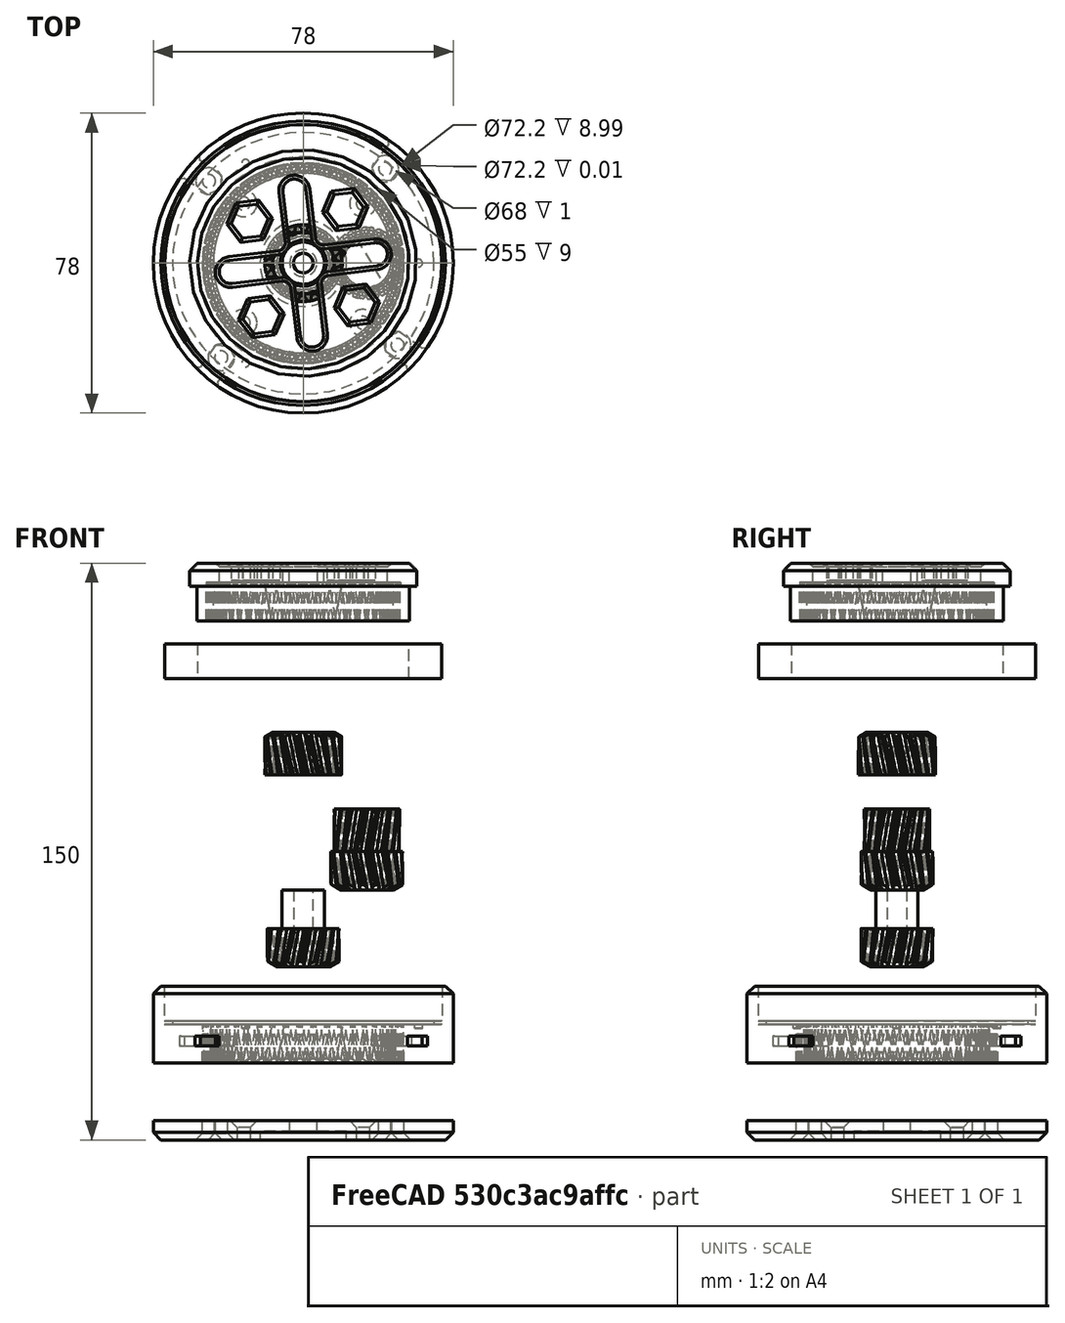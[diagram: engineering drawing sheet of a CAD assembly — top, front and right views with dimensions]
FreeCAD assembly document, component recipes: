
FREECAD ASSEMBLY — COMPONENT RECIPES ("gearbox-v3-helical")

This assembly document has 8 components, labeled P0..P7 below (a component is one placed body or linked part). 8 of them carry a construction recipe — the FreeCAD feature program that regenerates the part from scratch, quoted from this document or its linked companion documents; the rest are supplied as boundary geometry only. No exploded tour is included for this assembly.
COMPONENT P0 — recipe-attached ("S1-Sun", modeled in this document).
Construction recipe (the document's own serialized feature program — sketch geometry with constraints, then the solid features built on it; lengths are millimeters unless a unit is written):

FEATURE [Sketcher::SketchObject] Sketch008
  FullyConstrained = true
  MapMode = 5
  Support = -> [XY_Plane]
  TreeRank = 144
  sketch-geometry (1):
    g0: Circle CenterX=0 CenterY=0 CenterZ=0 NormalX=0 NormalY=0 NormalZ=1 AngleXU=0 Radius=2.55
  constraints (2):
    c: Coincident(g0,g-1)
    c: Diameter(g0) = 5.1
FEATURE [Part::Part2DObjectPython] InvoluteGear  label="s1-sun-gear"  # Draft 2D object (typed FeaturePython)
  ExternalGear = true
  HighPrecision = false
  Modules = 1.1
  NumberOfTeeth = 15
  PressureAngle = 20
  TreeRank = 283
  expr: Modules = <<sp>>.s1_module
  expr: NumberOfTeeth = <<sp>>.s1sun_teeth
FEATURE [PartDesign::AdditiveHelix] Helix003
  AddSubType = 0
  Angle = 0
  Axis = (-3e-16,3e-16,1)
  Base = (0,0,0)
  ClaimChildren = false
  Fit = 0
  FitJoin = 0
  Growth = 0
  HasBeenEdited = true
  Height = 10
  InnerFit = 0
  InnerFitJoin = 0
  LeftHanded = false
  Linearize = true
  Mode = 0
  NewSolid = false
  Outside = false
  Pitch = 250
  Profile = -> InvoluteGear
  ReferenceAxis = -> Z_Axis
  Suppress = false
  TreeRank = 284
  Turns = 0.04
  _ProfileBasedVersion = 1
FEATURE [PartDesign::Pocket] Pocket005
  AddSubType = 1
  BaseFeature = -> Helix003
  CheckUpToFaceLimits = true
  ClaimChildren = false
  Fit = 0
  FitJoin = 0
  InnerFit = 0
  InnerFitJoin = 0
  InnerTaperAngle = 0
  InnerTaperAngleRev = 0
  Length = 20
  Length2 = 20
  Linearize = true
  NewSolid = false
  Profile = -> Sketch008
  Reversed = true
  Suppress = false
  TreeRank = 145
  Type = 4
  _ProfileBasedVersion = 1
  _Version = 1
FEATURE [Sketcher::SketchObject] Sketch009
  FullyConstrained = true
  MapMode = 5
  Placement = pos=(3.3597e-05,5.68264e-05,10) rot=(-0.860809,0.508928,-1e-06;7e-06rad)
  Support = -> [Pocket005]
  TreeRank = 146
  sketch-geometry (2):
    g0: Circle CenterX=0 CenterY=0 CenterZ=0 NormalX=0 NormalY=0 NormalZ=1 AngleXU=0 Radius=2.55
    g1: Circle CenterX=0 CenterY=0 CenterZ=0 NormalX=0 NormalY=0 NormalZ=1 AngleXU=0 Radius=5.5
  constraints (4):
    c: Coincident(g0,g-1)
    c: Coincident(g1,g0)
    c: Diameter(g0) = 5.1
    c: Diameter(g1) = 11
FEATURE [PartDesign::Pad] Pad007
  AddSubType = 0
  AlongSketchNormal = false
  BaseFeature = -> Pocket005
  CheckUpToFaceLimits = true
  ClaimChildren = false
  Direction = (3.3597e-06,5.68264e-06,1)
  Fit = 0
  FitJoin = 0
  InnerFit = 0
  InnerFitJoin = 0
  InnerTaperAngle = 0
  InnerTaperAngleRev = 0
  Length = 10
  Length2 = 100
  Linearize = true
  NewSolid = false
  Profile = -> Sketch009
  Suppress = false
  TreeRank = 147
  Type = 0
  _ProfileBasedVersion = 1
FEATURE [Sketcher::SketchObject] Sketch025
  FullyConstrained = true
  MapMode = 5
  Placement = pos=(0,0,0) rot=(1,0,0;1.5708rad)
  Support = -> [XZ_Plane]
  TreeRank = 292
  sketch-geometry (4):
    g0: LineSegment StartX=9.36 StartY=0 StartZ=0 EndX=9.36 EndY=1.4376 EndZ=0
    g1: LineSegment StartX=9.36 StartY=1.4376 StartZ=0 EndX=6.87 EndY=0 EndZ=0
    g2: LineSegment StartX=6.87 StartY=0 StartZ=0 EndX=8.25 EndY=0 EndZ=0
    g3: LineSegment StartX=8.25 StartY=0 StartZ=0 EndX=9.36 EndY=0 EndZ=0
  constraints (12):
    c: PointOnObject(g2,g-1)
    c: PointOnObject(g3,g-1)
    c: Coincident(g3,g0)
    c: Vertical(g0)
    c: Coincident(g0,g1)
    c: Coincident(g1,g2)
    c: Coincident(g2,g3)
    c: PointOnObject(g2,g-1)
    c: Distance(g2) = 1.38  'm*1.25'
    c: Distance(g3) = 1.11  'm'
    c: Angle(g2,g1) = 0.523599  'chamfer_angle'
    c: Distance(g-1,g2) = 8.25  'm*z'
FEATURE [PartDesign::Groove] Groove001
  AddSubType = 1
  Angle = 360
  Axis = (0,-2e-16,1)
  Base = (0,0,0)
  BaseFeature = -> Pad007
  ClaimChildren = false
  Fit = 0
  FitJoin = 0
  InnerFit = 0
  InnerFitJoin = 0
  Linearize = true
  NewSolid = false
  Profile = -> Sketch025
  ReferenceAxis = -> Sketch025 [V_Axis]
  Suppress = false
  TreeRank = 293
  _ProfileBasedVersion = 1
FEATURE [PartDesign::Body] Body  label="S1-Sun"
  AutoGroupSolids = false
  ClaimAllChildren = false
  ExportMode = 0
  Group = -> [InvoluteGear,Sketch008,Helix003,Pocket005,Sketch009,Pad007,Sketch025,Groove001]
  Origin = -> Origin
  Placement = pos=(0,0,25) rot=(0,0,1;0rad)
  Tip = -> Groove001
  TreeRank = 64
  _ExportChildren = -> [Helix003,Pocket005,Pad007,Groove001]
  _GroupVersion = 1
COMPONENT P1 — recipe-attached ("S1-Ring", modeled in this document).
Construction recipe (the document's own serialized feature program — sketch geometry with constraints, then the solid features built on it; lengths are millimeters unless a unit is written):

FEATURE [Part::Part2DObjectPython] InvoluteGear001  label="s1-ring-outline"  # Draft 2D object (typed FeaturePython)
  ExternalGear = false
  HighPrecision = false
  Modules = 1.1
  NumberOfTeeth = 45
  PressureAngle = 20
  TreeRank = 2
  expr: Modules = <<sp>>.s1_module
  expr: NumberOfTeeth = <<sp>>.s1ring_teeth
FEATURE [Sketcher::SketchObject] Sketch
  FullyConstrained = true
  MapMode = 5
  Support = -> [XY_Plane001]
  TreeRank = 33
  sketch-geometry (1):
    g0: Circle CenterX=0 CenterY=0 CenterZ=0 NormalX=0 NormalY=0 NormalZ=1 AngleXU=0 Radius=39
  constraints (2):
    c: Coincident(g0,g-1)
    c: Diameter(g0) = 78  'outer_diameter'
FEATURE [PartDesign::Pad] Pad001
  AddSubType = 0
  AlongSketchNormal = false
  CheckUpToFaceLimits = true
  ClaimChildren = false
  Direction = (0,0,1)
  Fit = 0
  FitJoin = 0
  InnerFit = 0
  InnerFitJoin = 0
  InnerTaperAngle = 0
  InnerTaperAngleRev = 0
  Length = 9.99
  Length2 = 0
  Linearize = true
  NewSolid = false
  Profile = -> Sketch
  Suppress = false
  TreeRank = 34
  Type = 0
  _ProfileBasedVersion = 1
FEATURE [Sketcher::SketchObject] Sketch013
  FullyConstrained = true
  MapMode = 5
  Placement = pos=(0,0,10) rot=(0,0,1;0rad)
  TreeRank = 226
  sketch-geometry (2):
    g0: Circle CenterX=0 CenterY=0 CenterZ=0 NormalX=0 NormalY=0 NormalZ=1 AngleXU=0 Radius=34
    g1: Circle CenterX=0 CenterY=0 CenterZ=0 NormalX=0 NormalY=0 NormalZ=1 AngleXU=0 Radius=36.1
  constraints (4):
    c: Coincident(g0,g-1)
    c: Diameter(g0) = 68
    c: Coincident(g1,g0)
    c: Diameter(g1) = 72.2
FEATURE [PartDesign::SubtractiveHelix] Helix004
  AddSubType = 1
  Angle = 0
  Axis = (-3e-16,3e-16,1)
  Base = (0,0,0)
  BaseFeature = -> Pad001
  ClaimChildren = false
  Fit = 0
  FitJoin = 0
  Growth = 0
  HasBeenEdited = true
  Height = 10
  InnerFit = 0
  InnerFitJoin = 0
  LeftHanded = true
  Linearize = true
  Mode = 0
  NewSolid = false
  Outside = false
  Pitch = 750
  Profile = -> InvoluteGear001
  ReferenceAxis = -> Z_Axis001
  Suppress = false
  TreeRank = 285
  Turns = 0.0133333
  _ProfileBasedVersion = 1
FEATURE [PartDesign::Pad] Pad012
  AddSubType = 0
  AlongSketchNormal = false
  BaseFeature = -> Helix004
  CheckUpToFaceLimits = true
  ClaimChildren = false
  Direction = (0,0,1)
  Fit = 0
  FitJoin = 0
  InnerFit = 0
  InnerFitJoin = 0
  InnerTaperAngle = 0
  InnerTaperAngleRev = 0
  Length = 1
  Length2 = 100
  Linearize = true
  NewSolid = false
  Profile = -> Sketch013
  Suppress = false
  TreeRank = 227
  Type = 0
  _ProfileBasedVersion = 1
FEATURE [Sketcher::SketchObject] Sketch014
  FullyConstrained = true
  MapMode = 5
  Placement = pos=(0,0,9.99) rot=(0,0,1;0rad)
  Support = -> [Pad012]
  TreeRank = 228
  sketch-geometry (2):
    g0: Circle CenterX=0 CenterY=0 CenterZ=0 NormalX=0 NormalY=0 NormalZ=1 AngleXU=0 Radius=36.1
    g1: Circle CenterX=0 CenterY=0 CenterZ=0 NormalX=0 NormalY=0 NormalZ=1 AngleXU=0 Radius=39
  constraints (4):
    c: Coincident(g0,g-1)
    c: Diameter(g0) = 72.2
    c: Coincident(g1,g0)
    c: Diameter(g1) = 78
FEATURE [PartDesign::Pad] Pad013
  AddSubType = 0
  AlongSketchNormal = false
  CheckUpToFaceLimits = true
  ClaimChildren = false
  Direction = (0,0,1)
  Fit = 0
  FitJoin = 0
  InnerFit = 0
  InnerFitJoin = 0
  InnerTaperAngle = 0
  InnerTaperAngleRev = 0
  Length = 10
  Length2 = 100
  Linearize = true
  NewSolid = false
  Profile = -> Sketch014
  Suppress = false
  TreeRank = 229
  Type = 0
  _ProfileBasedVersion = 1
FEATURE [Sketcher::SketchObject] Sketch018
  FullyConstrained = true
  MapMode = 5
  Placement = pos=(0,0,0) rot=(1,0,0;3.14159rad)
  Support = -> [Pad013]
  TreeRank = 254
  sketch-geometry (11):
    g0: Circle [constr] CenterX=0 CenterY=0 CenterZ=0 NormalX=0 NormalY=0 NormalZ=1 AngleXU=0 Radius=32.5
    g1: GeomPoint [constr] X=0 Y=0 Z=0
    g2: LineSegment [constr] StartX=22.981 StartY=22.981 StartZ=0 EndX=-22.981 EndY=22.981 EndZ=0
    g3: LineSegment [constr] StartX=-22.981 StartY=22.981 StartZ=0 EndX=-22.981 EndY=-22.981 EndZ=0
    g4: LineSegment [constr] StartX=-22.981 StartY=-22.981 StartZ=0 EndX=22.981 EndY=-22.981 EndZ=0
    g5: LineSegment [constr] StartX=22.981 StartY=-22.981 StartZ=0 EndX=22.981 EndY=22.981 EndZ=0
    g6: Circle [constr] CenterX=0 CenterY=0 CenterZ=0 NormalX=0 NormalY=0 NormalZ=1 AngleXU=0 Radius=32.5
    g7: Circle CenterX=-22.981 CenterY=22.981 CenterZ=0 NormalX=0 NormalY=0 NormalZ=1 AngleXU=0 Radius=2.5
    g8: Circle CenterX=22.981 CenterY=22.981 CenterZ=0 NormalX=0 NormalY=0 NormalZ=1 AngleXU=0 Radius=2.5
    g9: Circle CenterX=22.981 CenterY=-22.981 CenterZ=0 NormalX=0 NormalY=0 NormalZ=1 AngleXU=0 Radius=2.5
    g10: Circle CenterX=-22.981 CenterY=-22.981 CenterZ=0 NormalX=0 NormalY=0 NormalZ=1 AngleXU=0 Radius=2.5
  constraints (25):
    c: Coincident(g0,g-1)
    c: Diameter(g0) = 65
    c: Coincident(g1,g0)
    c: Coincident(g2,g3)
    c: Coincident(g3,g4)
    c: Coincident(g4,g5)
    c: Coincident(g5,g2)
    c: Equal(g2,g3)
    c: Equal(g2,g4)
    c: Equal(g2,g5)
    c: PointOnObject(g2,g6)
    c: PointOnObject(g3,g6)
    c: PointOnObject(g4,g6)
    c: PointOnObject(g5,g6)
    c: Coincident(g6,g0)
    c: PointOnObject(g5,g0)
    c: Horizontal(g2)
    c: Coincident(g7,g2)
    c: Coincident(g8,g2)
    c: Coincident(g9,g4)
    c: Coincident(g10,g3)
    c: Equal(g7,g8)
    c: Equal(g8,g9)
    c: Equal(g9,g10)
    c: Diameter(g8) = 5
FEATURE [PartDesign::Hole] Hole001
  AddSubType = 1
  BaseFeature = -> Pad013
  ClaimChildren = false
  CustomThreadClearance = 0
  Depth = 7
  DepthType = 0
  Diameter = 3.4
  DrillForDepth = false
  DrillPoint = 0
  DrillPointAngle = 118
  Fit = 0
  FitJoin = 0
  HoleCutCountersinkAngle = 90
  HoleCutCustomValues = false
  HoleCutDepth = 0
  HoleCutDiameter = 6.1
  HoleCutType = 0
  InnerFit = 0
  InnerFitJoin = 0
  Linearize = true
  ModelThread = false
  NewSolid = false
  Profile = -> Sketch018
  Suppress = false
  Tapered = false
  TaperedAngle = 90
  ThreadClass = 0
  ThreadDepth = 7
  ThreadDepthType = 0
  ThreadDirection = 0
  ThreadFit = 0
  ThreadSize = 9
  ThreadType = 1
  Threaded = false
  TreeRank = 255
  UseCustomThreadClearance = false
  _ProfileBasedVersion = 1
FEATURE [PartDesign::Chamfer] Chamfer001
  AddSubType = 0
  Angle = 45
  Base = -> Hole001 [Edge279]
  BaseFeature = -> Hole001
  ChamferType = 0
  FlipDirection = false
  NewSolid = false
  Size = 2
  Size2 = 1
  SupportTransform = false
  Suppress = false
  TreeRank = 263
FEATURE [Sketcher::SketchObject] Sketch021
  AttachmentOffset = pos=(0,0,-4.4) rot=(0,0,1;0rad)
  FullyConstrained = true
  MapMode = 5
  Placement = pos=(0,0,4.4) rot=(1,0,0;3.14159rad)
  Support = -> [Chamfer001]
  TreeRank = 271
  sketch-geometry (15):
    g0: LineSegment [constr] StartX=22.98 StartY=22.98 StartZ=0 EndX=-22.98 EndY=22.98 EndZ=0
    g1: LineSegment [constr] StartX=-22.98 StartY=22.98 StartZ=0 EndX=-22.98 EndY=-22.98 EndZ=0
    g2: LineSegment [constr] StartX=-22.98 StartY=-22.98 StartZ=0 EndX=22.98 EndY=-22.98 EndZ=0
    g3: LineSegment [constr] StartX=22.98 StartY=-22.98 StartZ=0 EndX=22.98 EndY=22.98 EndZ=0
    g4: Circle [constr] CenterX=0 CenterY=0 CenterZ=0 NormalX=0 NormalY=0 NormalZ=1 AngleXU=0 Radius=32.4986
    g5: LineSegment StartX=-24.2068 StartY=19.6787 StartZ=0 EndX=-33.7711 EndY=31.2339 EndZ=0
    g6: LineSegment StartX=-33.7711 StartY=31.2339 StartZ=0 EndX=-29.072 EndY=35.1235 EndZ=0
    g7: LineSegment StartX=-29.072 StartY=35.1235 StartZ=0 EndX=-19.5076 EndY=23.5682 EndZ=0
    g8: LineSegment StartX=-20.7344 StartY=20.267 StartZ=0 EndX=-19.5076 EndY=23.5682 EndZ=0
    g9: LineSegment [constr] StartX=-19.5076 StartY=23.5682 StartZ=0 EndX=-21.7532 EndY=26.2813 EndZ=0
    g10: LineSegment [constr] StartX=-21.7532 StartY=26.2813 StartZ=0 EndX=-25.2256 EndY=25.693 EndZ=0
    g11: LineSegment [constr] StartX=-25.2256 StartY=25.693 StartZ=0 EndX=-26.4524 EndY=22.3918 EndZ=0
    g12: LineSegment [constr] StartX=-26.4524 StartY=22.3918 StartZ=0 EndX=-24.2068 EndY=19.6787 EndZ=0
    g13: LineSegment StartX=-24.2068 StartY=19.6787 StartZ=0 EndX=-20.7344 EndY=20.267 EndZ=0
    g14: Circle [constr] CenterX=-22.98 CenterY=22.98 CenterZ=0 NormalX=0 NormalY=0 NormalZ=1 AngleXU=0 Radius=3.52184
  constraints (38):
    c: Coincident(g0,g1)
    c: Coincident(g1,g2)
    c: Coincident(g2,g3)
    c: Coincident(g3,g0)
    c: Equal(g0,g1)
    c: Equal(g0,g2)
    c: Equal(g0,g3)
    c: PointOnObject(g0,g4)
    c: PointOnObject(g1,g4)
    c: PointOnObject(g2,g4)
    c: PointOnObject(g3,g4)
    c: Coincident(g4,g-1)
    c: Horizontal(g0)
    c: Distance(g0) = 45.96
    c: Coincident(g5,g6)
    c: Coincident(g6,g7)
    c: Perpendicular(g7,g6)
    c: Perpendicular(g5,g6)
    c: Distance(g7) = 15
    c: Distance(g6) = 6.1
    c: Coincident(g8,g9)
    c: Coincident(g9,g10)
    c: Coincident(g10,g11)
    c: Coincident(g11,g12)
    c: Coincident(g12,g13)
    c: Coincident(g13,g8)
    c: Equal(g8, g9-g13) x5
    c: PointOnObject(g8,g14)
    c: PointOnObject(g9,g14)
    c: PointOnObject(g10,g14)
    c: PointOnObject(g11,g14)
    c: PointOnObject(g12,g14)
    c: PointOnObject(g13,g14)
    c: Coincident(g14,g0)
    c: Parallel(g9,g7)
    c: Perpendicular(g4,g9)
    c: Coincident(g7,g8)
    c: Coincident(g5,g13)
FEATURE [PartDesign::Pocket] Pocket011
  AddSubType = 1
  BaseFeature = -> Chamfer001
  CheckUpToFaceLimits = true
  ClaimChildren = false
  Fit = 0
  FitJoin = 0
  InnerFit = 0
  InnerFitJoin = 0
  InnerTaperAngle = 0
  InnerTaperAngleRev = 0
  Length = 2.6
  Length2 = 3
  Linearize = true
  NewSolid = false
  Profile = -> Sketch021
  Suppress = false
  TreeRank = 272
  Type = 0
  _ProfileBasedVersion = 1
  _Version = 1
FEATURE [PartDesign::PolarPattern] PolarPattern
  AddSubType = 0
  Angle = 360
  Axis = -> Sketch021 [N_Axis]
  BaseFeature = -> Pocket011
  CopyShape = false
  NewSolid = false
  Occurrences = 4
  OriginalSubs = -> [Pocket011]
  Originals = -> [Pocket011]
  ParallelTransform = true
  SubTransform = true
  Suppress = false
  TreeRank = 278
  _Version = 3
FEATURE [PartDesign::Chamfer] Chamfer004
  AddSubType = 0
  Angle = 45
  Base = -> PolarPattern [Edge17,Edge18,Edge13,Edge15,Edge11,Edge9,Edge23,Edge21]
  BaseFeature = -> PolarPattern
  ChamferType = 0
  FlipDirection = false
  NewSolid = false
  Size = 1
  Size2 = 1
  SupportTransform = false
  Suppress = false
  TreeRank = 279
FEATURE [Sketcher::SketchObject] Sketch022
  FullyConstrained = true
  MapMode = 5
  Placement = pos=(0,0,9.99) rot=(0,0,1;0rad)
  Support = -> [Pad012]
  TreeRank = 287
  sketch-geometry (7):
    g0: Circle [constr] CenterX=0 CenterY=0 CenterZ=0 NormalX=0 NormalY=0 NormalZ=1 AngleXU=0 Radius=30
    g1: Circle CenterX=-13.1511 CenterY=26.9638 CenterZ=0 NormalX=0 NormalY=0 NormalZ=1 AngleXU=0 Radius=1
    g2: Circle CenterX=29.9269 CenterY=-2.09269 CenterZ=0 NormalX=0 NormalY=0 NormalZ=1 AngleXU=0 Radius=1
    g3: Circle CenterX=-16.7758 CenterY=-24.8711 CenterZ=0 NormalX=0 NormalY=0 NormalZ=1 AngleXU=0 Radius=1
    g4: LineSegment [constr] StartX=-13.1511 StartY=26.9638 StartZ=0 EndX=0 EndY=0 EndZ=0
    g5: LineSegment [constr] StartX=29.9269 StartY=-2.09269 StartZ=0 EndX=0 EndY=0 EndZ=0
    g6: LineSegment [constr] StartX=0 StartY=0 StartZ=0 EndX=-16.7758 EndY=-24.8711 EndZ=0
  constraints (17):
    c: Coincident(g0,g-1)
    c: Diameter(g0) = 60
    c: PointOnObject(g1,g0)
    c: PointOnObject(g2,g0)
    c: PointOnObject(g3,g0)
    c: Equal(g1,g2)
    c: Equal(g2,g3)
    c: Diameter(g1) = 2
    c: Coincident(g4,g1)
    c: Coincident(g4,g0)
    c: Coincident(g5,g2)
    c: Coincident(g5,g0)
    c: Coincident(g6,g0)
    c: Coincident(g6,g3)
    c: Angle(g5,g4) = 2.0944
    c: Angle(g6,g5) = 2.0944
    c: Angle(g5,g-1) = 0.0698132
FEATURE [PartDesign::Pocket] Pocket
  AddSubType = 1
  BaseFeature = -> Chamfer004
  CheckUpToFaceLimits = true
  ClaimChildren = false
  Fit = 0
  FitJoin = 0
  InnerFit = 0
  InnerFitJoin = 0
  InnerTaperAngle = 0
  InnerTaperAngleRev = 0
  Length = 1
  Length2 = 100
  Linearize = true
  NewSolid = false
  Profile = -> Sketch022
  Suppress = false
  TreeRank = 288
  Type = 0
  _ProfileBasedVersion = 1
  _Version = 1
FEATURE [Sketcher::SketchObject] Sketch026
  FullyConstrained = true
  MapMode = 5
  Placement = pos=(0,0,0) rot=(1,0,0;1.5708rad)
  Support = -> [XZ_Plane001]
  TreeRank = 294
  sketch-geometry (4):
    g0: LineSegment StartX=26.13 StartY=0 StartZ=0 EndX=23.65 EndY=1.43183 EndZ=0
    g1: LineSegment StartX=23.65 StartY=1.43183 StartZ=0 EndX=23.65 EndY=0 EndZ=0
    g2: LineSegment StartX=23.65 StartY=0 StartZ=0 EndX=24.75 EndY=0 EndZ=0
    g3: LineSegment StartX=24.75 StartY=0 StartZ=0 EndX=26.13 EndY=0 EndZ=0
  constraints (12):
    c: PointOnObject(g2,g-1)
    c: Coincident(g3,g0)
    c: Coincident(g0,g1)
    c: Coincident(g1,g2)
    c: Distance(g2) = 1.1  'm*1.25'
    c: Distance(g3) = 1.38  'm'
    c: Vertical(g1)
    c: Angle(g0,g3) = 0.523599
    c: PointOnObject(g0,g-1)
    c: Coincident(g2,g3)
    c: PointOnObject(g2,g-1)
    c: DistanceX(g-1,g2) = 24.75
FEATURE [PartDesign::Groove] Groove002
  AddSubType = 1
  Angle = 360
  Axis = (0,-2e-16,1)
  Base = (0,0,0)
  BaseFeature = -> Pocket
  ClaimChildren = false
  Fit = 0
  FitJoin = 0
  InnerFit = 0
  InnerFitJoin = 0
  Linearize = true
  NewSolid = false
  Profile = -> Sketch026
  ReferenceAxis = -> Sketch026 [V_Axis]
  Suppress = false
  TreeRank = 295
  _ProfileBasedVersion = 1
FEATURE [PartDesign::Body] Body001  label="S1-Ring"
  AutoGroupSolids = false
  ClaimAllChildren = false
  ExportMode = 0
  Group = -> [Sketch,Pad001,InvoluteGear001,Sketch013,Helix004,Pad012,Sketch014,Pad013,Sketch018,Hole001,Chamfer001,Sketch021,Pocket011,PolarPattern,Chamfer004,Sketch022,Pocket,Sketch026,Groove002]
  Origin = -> Origin001
  Placement = pos=(0,0,0) rot=(0,0,1;0.069813rad)
  Tip = -> Groove002
  TreeRank = 60
  _ExportChildren = -> [Pad001,Helix004,Pad012,Pad013,Hole001,Chamfer001,Pocket011,PolarPattern,Chamfer004,Pocket,Groove002]
  _GroupVersion = 1
COMPONENT P2 — recipe-attached ("S2-Ring", modeled in this document).
Construction recipe (the document's own serialized feature program — sketch geometry with constraints, then the solid features built on it; lengths are millimeters unless a unit is written):

FEATURE [Part::Part2DObjectPython] InvoluteGear003  label="s2-ring-gear"  # Draft 2D object (typed FeaturePython)
  ExternalGear = false
  HighPrecision = false
  Modules = 1
  NumberOfTeeth = 48
  PressureAngle = 20
  TreeRank = 58
  expr: Modules = <<sp>>.s2_module
  expr: NumberOfTeeth = <<sp>>.s2ring_teeth
FEATURE [Sketcher::SketchObject] Sketch001
  FullyConstrained = true
  MapMode = 5
  Support = -> [XY_Plane002]
  TreeRank = 87
  sketch-geometry (1):
    g0: Circle CenterX=0 CenterY=0 CenterZ=0 NormalX=0 NormalY=0 NormalZ=1 AngleXU=0 Radius=27.65
  constraints (2):
    c: Coincident(g0,g-1)
    c: Diameter(g0) = 55.3  'outer_diameter'
FEATURE [PartDesign::Pad] Pad002
  AddSubType = 0
  AlongSketchNormal = false
  CheckUpToFaceLimits = true
  ClaimChildren = false
  Direction = (0,0,1)
  Fit = 0
  FitJoin = 0
  InnerFit = 0
  InnerFitJoin = 0
  InnerTaperAngle = 0
  InnerTaperAngleRev = 0
  Length = 15
  Length2 = 0
  Linearize = true
  NewSolid = false
  Profile = -> Sketch001
  Suppress = false
  TreeRank = 88
  Type = 0
  _ProfileBasedVersion = 1
FEATURE [Sketcher::SketchObject] Sketch012
  FullyConstrained = true
  MapMode = 5
  Placement = pos=(0,0,15) rot=(0,0,1;0rad)
  TreeRank = 224
  sketch-geometry (2):
    g0: Circle CenterX=0 CenterY=0 CenterZ=0 NormalX=0 NormalY=0 NormalZ=1 AngleXU=0 Radius=27.65
    g1: Circle CenterX=0 CenterY=0 CenterZ=0 NormalX=0 NormalY=0 NormalZ=1 AngleXU=0 Radius=29.5
  constraints (4):
    c: Coincident(g0,g-1)
    c: Diameter(g0) = 55.3
    c: Coincident(g1,g0)
    c: Diameter(g1) = 59
FEATURE [Sketcher::SketchObject] Sketch019
  FullyConstrained = true
  MapMode = 5
  Placement = pos=(0,0,15) rot=(0,0,1;0rad)
  TreeRank = 258
  sketch-geometry (33):
    g0: LineSegment [constr] StartX=-12.5 StartY=-12.5 StartZ=0 EndX=-12.5 EndY=12.5 EndZ=0
    g1: LineSegment [constr] StartX=-12.5 StartY=12.5 StartZ=0 EndX=12.5 EndY=12.5 EndZ=0
    g2: LineSegment [constr] StartX=12.5 StartY=12.5 StartZ=0 EndX=12.5 EndY=-12.5 EndZ=0
    g3: LineSegment [constr] StartX=12.5 StartY=-12.5 StartZ=0 EndX=-12.5 EndY=-12.5 EndZ=0
    g4: GeomPoint [constr] X=0 Y=0 Z=0
    g5: LineSegment StartX=-14.9 StartY=16.6569 StartZ=0 EndX=-17.3 EndY=12.5 EndZ=0
    g6: LineSegment StartX=-17.3 StartY=12.5 StartZ=0 EndX=-14.9 EndY=8.34308 EndZ=0
    g7: LineSegment StartX=-14.9 StartY=8.34308 StartZ=0 EndX=-10.1 EndY=8.34308 EndZ=0
    g8: LineSegment StartX=-10.1 StartY=8.34308 StartZ=0 EndX=-7.7 EndY=12.5 EndZ=0
    g9: LineSegment StartX=-7.7 StartY=12.5 StartZ=0 EndX=-10.1 EndY=16.6569 EndZ=0
    g10: LineSegment StartX=-10.1 StartY=16.6569 StartZ=0 EndX=-14.9 EndY=16.6569 EndZ=0
    g11: Circle [constr] CenterX=-12.5 CenterY=12.5 CenterZ=0 NormalX=0 NormalY=0 NormalZ=1 AngleXU=0 Radius=4.8
    g12: LineSegment StartX=10.1 StartY=16.6569 StartZ=0 EndX=7.7 EndY=12.5 EndZ=0
    g13: LineSegment StartX=7.7 StartY=12.5 StartZ=0 EndX=10.1 EndY=8.34308 EndZ=0
    g14: LineSegment StartX=10.1 StartY=8.34308 StartZ=0 EndX=14.9 EndY=8.34308 EndZ=0
    g15: LineSegment StartX=14.9 StartY=8.34308 StartZ=0 EndX=17.3 EndY=12.5 EndZ=0
    g16: LineSegment StartX=17.3 StartY=12.5 StartZ=0 EndX=14.9 EndY=16.6569 EndZ=0
    g17: LineSegment StartX=14.9 StartY=16.6569 StartZ=0 EndX=10.1 EndY=16.6569 EndZ=0
    g18: Circle [constr] CenterX=12.5 CenterY=12.5 CenterZ=0 NormalX=0 NormalY=0 NormalZ=1 AngleXU=0 Radius=4.8
    g19: LineSegment StartX=10.1 StartY=-8.34308 StartZ=0 EndX=7.7 EndY=-12.5 EndZ=0
    g20: LineSegment StartX=7.7 StartY=-12.5 StartZ=0 EndX=10.1 EndY=-16.6569 EndZ=0
    g21: LineSegment StartX=10.1 StartY=-16.6569 StartZ=0 EndX=14.9 EndY=-16.6569 EndZ=0
    g22: LineSegment StartX=14.9 StartY=-16.6569 StartZ=0 EndX=17.3 EndY=-12.5 EndZ=0
    g23: LineSegment StartX=17.3 StartY=-12.5 StartZ=0 EndX=14.9 EndY=-8.34308 EndZ=0
    g24: LineSegment StartX=14.9 StartY=-8.34308 StartZ=0 EndX=10.1 EndY=-8.34308 EndZ=0
    g25: Circle [constr] CenterX=12.5 CenterY=-12.5 CenterZ=0 NormalX=0 NormalY=0 NormalZ=1 AngleXU=0 Radius=4.8
    g26: LineSegment StartX=-14.9 StartY=-8.34308 StartZ=0 EndX=-17.3 EndY=-12.5 EndZ=0
    g27: LineSegment StartX=-17.3 StartY=-12.5 StartZ=0 EndX=-14.9 EndY=-16.6569 EndZ=0
    g28: LineSegment StartX=-14.9 StartY=-16.6569 StartZ=0 EndX=-10.1 EndY=-16.6569 EndZ=0
    g29: LineSegment StartX=-10.1 StartY=-16.6569 StartZ=0 EndX=-7.7 EndY=-12.5 EndZ=0
    g30: LineSegment StartX=-7.7 StartY=-12.5 StartZ=0 EndX=-10.1 EndY=-8.34308 EndZ=0
    g31: LineSegment StartX=-10.1 StartY=-8.34308 StartZ=0 EndX=-14.9 EndY=-8.34308 EndZ=0
    g32: Circle [constr] CenterX=-12.5 CenterY=-12.5 CenterZ=0 NormalX=0 NormalY=0 NormalZ=1 AngleXU=0 Radius=4.8
  constraints (76):
    c: Coincident(g0,g1)
    c: Coincident(g1,g2)
    c: Coincident(g2,g3)
    c: Coincident(g3,g0)
    c: Horizontal(g1)
    c: Horizontal(g3)
    c: Vertical(g0)
    c: Vertical(g2)
    c: Symmetric(g1,g0,g4)
    c: Coincident(g4,g-1)
    c: Equal(g1,g2)
    c: Distance(g1) = 25
    c: Coincident(g5,g6)
    c: Coincident(g6,g7)
    c: Coincident(g7,g8)
    c: Coincident(g8,g9)
    c: Coincident(g9,g10)
    c: Coincident(g10,g5)
    c: Equal(g5, g6-g10) x5
    c: PointOnObject(g5,g11)
    c: PointOnObject(g6,g11)
    c: PointOnObject(g7,g11)
    c: PointOnObject(g8,g11)
    c: PointOnObject(g9,g11)
    c: PointOnObject(g10,g11)
    c: Coincident(g11,g0)
    c: Coincident(g12,g13)
    c: Coincident(g13,g14)
    c: Coincident(g14,g15)
    c: Coincident(g15,g16)
    c: Coincident(g16,g17)
    c: Coincident(g17,g12)
    c: Equal(g12, g13-g17) x5
    c: PointOnObject(g12,g18)
    c: PointOnObject(g13,g18)
    c: PointOnObject(g14,g18)
    c: PointOnObject(g15,g18)
    c: PointOnObject(g16,g18)
    c: PointOnObject(g17,g18)
    c: Coincident(g18,g1)
    c: Coincident(g19,g20)
    c: Coincident(g20,g21)
    c: Coincident(g21,g22)
    c: Coincident(g22,g23)
    c: Coincident(g23,g24)
    c: Coincident(g24,g19)
    c: Equal(g19, g20-g24) x5
    c: PointOnObject(g19,g25)
    c: PointOnObject(g20,g25)
    c: PointOnObject(g21,g25)
    c: PointOnObject(g22,g25)
    c: PointOnObject(g23,g25)
    c: PointOnObject(g24,g25)
    c: Coincident(g25,g2)
    c: Coincident(g26,g27)
    c: Coincident(g27,g28)
    c: Coincident(g28,g29)
    c: Coincident(g29,g30)
    c: Coincident(g30,g31)
    c: Coincident(g31,g26)
    c: Equal(g26, g27-g31) x5
    c: PointOnObject(g26,g32)
    c: PointOnObject(g27,g32)
    c: PointOnObject(g28,g32)
    c: PointOnObject(g29,g32)
    c: PointOnObject(g30,g32)
    c: PointOnObject(g31,g32)
    c: Coincident(g32,g0)
    c: Equal(g31,g10)
    c: Equal(g10,g17)
    c: Equal(g17,g24)
    c: Horizontal(g10)
    c: Horizontal(g17)
    c: Horizontal(g24)
    c: Horizontal(g31)
    c: Distance(g17) = 4.8
FEATURE [PartDesign::SubtractiveHelix] Helix005
  AddSubType = 1
  Angle = 0
  Axis = (-3e-16,3e-16,1)
  Base = (0,0,0)
  BaseFeature = -> Pad002
  ClaimChildren = false
  Fit = 0
  FitJoin = 0
  Growth = 0
  HasBeenEdited = true
  Height = 10
  InnerFit = 0
  InnerFitJoin = 0
  LeftHanded = false
  Linearize = true
  Mode = 0
  NewSolid = false
  Outside = false
  Pitch = 750
  Profile = -> InvoluteGear003
  ReferenceAxis = -> Z_Axis002
  Suppress = false
  TreeRank = 286
  Turns = 0.0133333
  _ProfileBasedVersion = 1
FEATURE [PartDesign::Pad] Pad011
  AddSubType = 0
  AlongSketchNormal = false
  BaseFeature = -> Helix005
  CheckUpToFaceLimits = true
  ClaimChildren = false
  Direction = (0,0,1)
  Fit = 0
  FitJoin = 0
  InnerFit = 0
  InnerFitJoin = 0
  InnerTaperAngle = 0
  InnerTaperAngleRev = 0
  Length = 6
  Length2 = 100
  Linearize = true
  NewSolid = false
  Profile = -> Sketch012
  Reversed = true
  Suppress = false
  TreeRank = 225
  Type = 0
  _ProfileBasedVersion = 1
FEATURE [PartDesign::Pocket] Pocket009
  AddSubType = 1
  BaseFeature = -> Pad011
  CheckUpToFaceLimits = true
  ClaimChildren = false
  Fit = 0
  FitJoin = 0
  InnerFit = 0
  InnerFitJoin = 0
  InnerTaperAngle = 0
  InnerTaperAngleRev = 0
  Length = 4.5
  Length2 = 100
  Linearize = true
  NewSolid = false
  Profile = -> Sketch019
  Suppress = false
  TreeRank = 259
  Type = 0
  _ProfileBasedVersion = 1
  _Version = 1
FEATURE [Sketcher::SketchObject] Sketch020
  FullyConstrained = true
  MapMode = 5
  Placement = pos=(0,0,15) rot=(0,0,1;0rad)
  Support = -> [Pocket009]
  TreeRank = 260
  sketch-geometry (21):
    g0: LineSegment StartX=-3 StartY=19 StartZ=0 EndX=-3 EndY=6 EndZ=0
    g1: LineSegment StartX=3 StartY=19 StartZ=0 EndX=3 EndY=6 EndZ=0
    g2: LineSegment StartX=6 StartY=3 StartZ=0 EndX=19 EndY=3 EndZ=0
    g3: LineSegment StartX=6 StartY=-3 StartZ=0 EndX=19 EndY=-3 EndZ=0
    g4: LineSegment StartX=-6 StartY=3 StartZ=0 EndX=-19 EndY=3 EndZ=0
    g5: LineSegment StartX=-19 StartY=-3 StartZ=0 EndX=-6 EndY=-3 EndZ=0
    g6: LineSegment StartX=-3 StartY=-6 StartZ=0 EndX=-3 EndY=-19 EndZ=0
    g7: LineSegment StartX=3 StartY=-6 StartZ=0 EndX=3 EndY=-19 EndZ=0
    g8: ArcOfCircle CenterX=-6 CenterY=6 CenterZ=0 NormalX=0 NormalY=0 NormalZ=1 AngleXU=0 Radius=3 StartAngle=4.71239 EndAngle=6.28319
    g9: ArcOfCircle CenterX=1e-16 CenterY=19 CenterZ=0 NormalX=0 NormalY=0 NormalZ=1 AngleXU=0 Radius=3 StartAngle=0 EndAngle=3.14159
    g10: ArcOfCircle CenterX=6 CenterY=6 CenterZ=0 NormalX=0 NormalY=0 NormalZ=1 AngleXU=0 Radius=3 StartAngle=3.14159 EndAngle=4.71239
    g11: ArcOfCircle CenterX=19 CenterY=-4e-16 CenterZ=0 NormalX=0 NormalY=0 NormalZ=1 AngleXU=0 Radius=3 StartAngle=4.71239 EndAngle=7.85398
    g12: ArcOfCircle CenterX=6 CenterY=-6 CenterZ=0 NormalX=0 NormalY=0 NormalZ=1 AngleXU=0 Radius=3 StartAngle=1.5708 EndAngle=3.14159
    g13: ArcOfCircle CenterX=-8e-16 CenterY=-19 CenterZ=0 NormalX=0 NormalY=0 NormalZ=1 AngleXU=0 Radius=3 StartAngle=3.14159 EndAngle=6.28319
    g14: ArcOfCircle CenterX=-6 CenterY=-6 CenterZ=0 NormalX=0 NormalY=0 NormalZ=1 AngleXU=0 Radius=3 StartAngle=0 EndAngle=1.5708
    g15: ArcOfCircle CenterX=-19 CenterY=4e-16 CenterZ=0 NormalX=0 NormalY=0 NormalZ=1 AngleXU=0 Radius=3 StartAngle=1.5708 EndAngle=4.71239
    g16: LineSegment [constr] StartX=-6 StartY=-6 StartZ=0 EndX=-6 EndY=6 EndZ=0
    g17: LineSegment [constr] StartX=-6 StartY=6 StartZ=0 EndX=6 EndY=6 EndZ=0
    g18: LineSegment [constr] StartX=6 StartY=6 StartZ=0 EndX=6 EndY=-6 EndZ=0
    g19: LineSegment [constr] StartX=6 StartY=-6 StartZ=0 EndX=-6 EndY=-6 EndZ=0
    g20: GeomPoint [constr] X=0 Y=0 Z=0
  constraints (52):
    c: Vertical(g0)
    c: Vertical(g1)
    c: Horizontal(g2)
    c: Horizontal(g3)
    c: Horizontal(g4)
    c: Horizontal(g5)
    c: Vertical(g6)
    c: Vertical(g7)
    c: Equal(g0,g1)
    c: Equal(g1,g2)
    c: Equal(g2,g3)
    c: Equal(g3,g4)
    c: Equal(g4,g5)
    c: Equal(g5,g6)
    c: Equal(g6,g7)
    c: Tangent(g4,g8) = 1.5708
    c: Tangent(g0,g9) = -1.5708
    c: Tangent(g1,g10) = -1.5708
    c: Tangent(g2,g11) = 1.5708
    c: Tangent(g3,g12) = 1.5708
    c: Coincident(g12,g7)
    c: Tangent(g7,g13) = 1.5708
    c: Tangent(g6,g14) = 1.5708
    c: Coincident(g14,g5)
    c: Tangent(g5,g15) = -1.5708
    c: Coincident(g15,g4)
    c: Equal(g15,g11)
    c: Equal(g11,g9)
    c: Equal(g9,g13)
    c: Equal(g13,g14)
    c: Equal(g14,g12)
    c: Equal(g12,g10)
    c: Equal(g10,g8)
    c: Tangent(g10,g2) = -1.5708
    c: Tangent(g8,g0) = 1.5708
    c: Tangent(g9,g1) = 1.5708
    c: Tangent(g13,g6) = -1.5708
    c: Tangent(g11,g3) = -1.5708
    c: Vertical(g4,g5)
    c: Coincident(g16,g17)
    c: Coincident(g17,g18)
    c: Coincident(g18,g19)
    c: Coincident(g19,g16)
    c: Horizontal(g17)
    c: Vertical(g16)
    c: Symmetric(g17,g16,g20)
    c: Coincident(g20,g-1)
    c: Coincident(g17,g10)
    c: Coincident(g18,g12)
    c: Coincident(g16,g14)
    c: Distance(g17) = 12
    c: Distance(g2) = 13
FEATURE [PartDesign::Pocket] Pocket010
  AddSubType = 1
  BaseFeature = -> Pocket009
  CheckUpToFaceLimits = true
  ClaimChildren = false
  Fit = 0
  FitJoin = 0
  InnerFit = 0
  InnerFitJoin = 0
  InnerTaperAngle = 0
  InnerTaperAngleRev = 0
  Length = 7
  Length2 = 100
  Linearize = true
  NewSolid = false
  Profile = -> Sketch020
  Suppress = false
  TreeRank = 261
  Type = 0
  _ProfileBasedVersion = 1
  _Version = 1
FEATURE [PartDesign::Chamfer] Chamfer
  AddSubType = 0
  Angle = 45
  Base = -> Pocket010 [Face311]
  BaseFeature = -> Pocket010
  ChamferType = 0
  FlipDirection = false
  NewSolid = false
  Size = 1
  Size2 = 1
  SupportTransform = false
  Suppress = false
  TreeRank = 274
FEATURE [PartDesign::Chamfer] Chamfer003
  AddSubType = 0
  Angle = 45
  Base = -> Chamfer [Edge972]
  BaseFeature = -> Chamfer
  ChamferType = 0
  FlipDirection = false
  NewSolid = false
  Size = 2
  Size2 = 1
  SupportTransform = false
  Suppress = false
  TreeRank = 275
FEATURE [PartDesign::Body] Body002  label="S2-Ring"
  AutoGroupSolids = false
  ClaimAllChildren = false
  ExportMode = 0
  Group = -> [Sketch001,Pad002,InvoluteGear003,Sketch012,Helix005,Pad011,Sketch019,Pocket009,Sketch020,Pocket010,Chamfer,Chamfer003]
  Origin = -> Origin002
  Placement = pos=(0,0,115) rot=(0,0,1;0.122173rad)
  Tip = -> Chamfer003
  TreeRank = 86
  _ExportChildren = -> [Pad002,Helix005,Pad011,Pocket009,Pocket010,Chamfer,Chamfer003]
  _GroupVersion = 1
COMPONENT P3 — recipe-attached ("S2-Sun", modeled in this document).
Construction recipe (the document's own serialized feature program — sketch geometry with constraints, then the solid features built on it; lengths are millimeters unless a unit is written):

FEATURE [Part::Part2DObjectPython] InvoluteGear002  label="s2-sun-gear"  # Draft 2D object (typed FeaturePython)
  ExternalGear = true
  HighPrecision = false
  Modules = 1
  NumberOfTeeth = 18
  PressureAngle = 20
  TreeRank = 42
  expr: Modules = <<sp>>.s2_module
  expr: NumberOfTeeth = <<sp>>.s2sun_teeth
FEATURE [Sketcher::SketchObject] Sketch010
  FullyConstrained = true
  MapMode = 5
  Placement = pos=(0,0,9) rot=(0,0,1;0rad)
  TreeRank = 164
  sketch-geometry (1):
    g0: Circle CenterX=0 CenterY=0 CenterZ=0 NormalX=0 NormalY=0 NormalZ=1 AngleXU=0 Radius=6
  constraints (2):
    c: Coincident(g0,g-1)
    c: Diameter(g0) = 12
FEATURE [PartDesign::AdditiveHelix] Helix
  AddSubType = 0
  Angle = 0
  Axis = (-3e-16,3e-16,1)
  Base = (0,0,0)
  ClaimChildren = false
  Fit = 0
  FitJoin = 0
  Growth = 0
  HasBeenEdited = true
  Height = 11
  InnerFit = 0
  InnerFitJoin = 0
  LeftHanded = true
  Linearize = true
  Mode = 0
  NewSolid = false
  Outside = false
  Pitch = 250
  Profile = -> InvoluteGear002
  ReferenceAxis = -> Z_Axis003
  Suppress = false
  TreeRank = 280
  Turns = 0.044
  _ProfileBasedVersion = 1
FEATURE [PartDesign::Pocket] Pocket006
  AddSubType = 1
  BaseFeature = -> Helix
  CheckUpToFaceLimits = true
  ClaimChildren = false
  Fit = 0
  FitJoin = 0
  InnerFit = 0
  InnerFitJoin = 0
  InnerTaperAngle = 0
  InnerTaperAngleRev = 0
  Length = 10
  Length2 = 10
  Linearize = true
  NewSolid = false
  Profile = -> Sketch010
  Suppress = false
  TreeRank = 165
  Type = 4
  _ProfileBasedVersion = 1
  _Version = 1
FEATURE [Sketcher::SketchObject] Sketch027
  FullyConstrained = true
  MapMode = 5
  Placement = pos=(0,0,0) rot=(1,0,0;1.5708rad)
  Support = -> [XZ_Plane003]
  TreeRank = 296
  sketch-geometry (4):
    g0: LineSegment StartX=10.25 StartY=11.01 StartZ=0 EndX=10.25 EndY=9.71096 EndZ=0
    g1: LineSegment StartX=10.25 StartY=9.71096 StartZ=0 EndX=8 EndY=11.01 EndZ=0
    g2: LineSegment StartX=8 StartY=11.01 StartZ=0 EndX=9 EndY=11.01 EndZ=0
    g3: LineSegment StartX=9 StartY=11.01 StartZ=0 EndX=10.25 EndY=11.01 EndZ=0
  constraints (12):
    c: Coincident(g3,g0)
    c: Vertical(g0)
    c: Coincident(g0,g1)
    c: Coincident(g1,g2)
    c: Coincident(g2,g3)
    c: Distance(g2) = 1  'm*1.25'
    c: Distance(g3) = 1.25  'm'
    c: DistanceX(g-1,g2) = 9
    c: Horizontal(g3)
    c: Horizontal(g2)
    c: Angle(g1,g3) = 0.523599
    c: DistanceY(g-1,g2) = 11.01
FEATURE [PartDesign::Groove] Groove003
  AddSubType = 1
  Angle = 360
  Axis = (0,-2e-16,1)
  Base = (0,0,0)
  BaseFeature = -> Pocket006
  ClaimChildren = false
  Fit = 0
  FitJoin = 0
  InnerFit = 0
  InnerFitJoin = 0
  Linearize = true
  NewSolid = false
  Profile = -> Sketch027
  ReferenceAxis = -> Sketch027 [V_Axis]
  Suppress = false
  TreeRank = 297
  _ProfileBasedVersion = 1
FEATURE [PartDesign::Body] Body003  label="S2-Sun"
  AutoGroupSolids = false
  ClaimAllChildren = false
  ExportMode = 0
  Group = -> [InvoluteGear002,Sketch010,Helix,Pocket006,Sketch027,Groove003]
  Origin = -> Origin003
  Placement = pos=(0,0,75) rot=(0,0,1;0.235619rad)
  Tip = -> Groove003
  TreeRank = 104
  _ExportChildren = -> [Helix,Pocket006,Groove003]
  _GroupVersion = 1
COMPONENT P4 — recipe-attached ("Bearing", modeled in this document).
Construction recipe (the document's own serialized feature program — sketch geometry with constraints, then the solid features built on it; lengths are millimeters unless a unit is written):

FEATURE [Sketcher::SketchObject] Sketch011
  FullyConstrained = true
  MapMode = 5
  Support = -> [XY_Plane006]
  TreeRank = 222
  sketch-geometry (2):
    g0: Circle CenterX=0 CenterY=0 CenterZ=0 NormalX=0 NormalY=0 NormalZ=1 AngleXU=0 Radius=27.5
    g1: Circle CenterX=0 CenterY=0 CenterZ=0 NormalX=0 NormalY=0 NormalZ=1 AngleXU=0 Radius=36
  constraints (4):
    c: Coincident(g0,g-1)
    c: Diameter(g0) = 55
    c: Coincident(g1,g0)
    c: Diameter(g1) = 72
FEATURE [PartDesign::Pad] Pad010
  AddSubType = 0
  AlongSketchNormal = false
  CheckUpToFaceLimits = true
  ClaimChildren = false
  Direction = (0,0,1)
  Fit = 0
  FitJoin = 0
  InnerFit = 0
  InnerFitJoin = 0
  InnerTaperAngle = 0
  InnerTaperAngleRev = 0
  Length = 9
  Length2 = 100
  Linearize = true
  NewSolid = false
  Profile = -> Sketch011
  Suppress = false
  TreeRank = 223
  Type = 0
  _ProfileBasedVersion = 1
FEATURE [PartDesign::Body] Body006  label="Bearing"
  AutoGroupSolids = false
  ClaimAllChildren = false
  ExportMode = 0
  Group = -> [Sketch011,Pad010]
  Origin = -> Origin006
  Placement = pos=(0,0,100) rot=(0,0,1;0rad)
  Tip = -> Pad010
  TreeRank = 221
  _ExportChildren = -> [Pad010]
  _GroupVersion = 1
COMPONENT P5 — recipe-attached ("Bottom-cap", modeled in this document).
Construction recipe (the document's own serialized feature program — sketch geometry with constraints, then the solid features built on it; lengths are millimeters unless a unit is written):

FEATURE [PartDesign::SubShapeBinder] Binder  label="Binder(Sketch018)"
  BindCopyOnChange = 0
  BindMode = 0
  ClaimChildren = false
  Context = -> Body007 [Binder.]
  FillStyle = 0
  Fuse = false
  MakeFace = true
  PartialLoad = false
  Placement = pos=(0,0,-20) rot=(0,0,1;0rad)
  Relative = true
  Support = -> [Body001[Sketch018.]]
  TreeRank = 256
  _Version = 8
FEATURE [PartDesign::ShapeBinder] ShapeBinder001
  Support = -> [Pad013]
  TraceSupport = false
  TreeRank = 246
FEATURE [PartDesign::Pad] Pad015
  AddSubType = 0
  AlongSketchNormal = false
  CheckUpToFaceLimits = true
  ClaimChildren = false
  Direction = (0,0,1)
  Fit = 0
  FitJoin = 0
  InnerFit = 0
  InnerFitJoin = 0
  InnerTaperAngle = 0
  InnerTaperAngleRev = 0
  Length = 5
  Length2 = 100
  Linearize = true
  NewSolid = false
  Profile = -> ShapeBinder001
  Reversed = true
  Suppress = false
  TreeRank = 247
  Type = 0
  _ProfileBasedVersion = 1
FEATURE [Sketcher::SketchObject] Sketch015
  FullyConstrained = true
  MapMode = 5
  Placement = pos=(0,0,-5) rot=(1,0,0;3.14159rad)
  Support = -> [Pad015]
  TreeRank = 248
  sketch-geometry (1):
    g0: Circle CenterX=0 CenterY=0 CenterZ=0 NormalX=0 NormalY=0 NormalZ=1 AngleXU=0 Radius=11.25
  constraints (2):
    c: Coincident(g0,g-1)
    c: Diameter(g0) = 22.5
FEATURE [PartDesign::Pocket] Pocket007
  AddSubType = 1
  BaseFeature = -> Pad015
  CheckUpToFaceLimits = true
  ClaimChildren = false
  Fit = 0
  FitJoin = 0
  InnerFit = 0
  InnerFitJoin = 0
  InnerTaperAngle = 0
  InnerTaperAngleRev = 0
  Length = 2.2
  Length2 = 100
  Linearize = true
  NewSolid = false
  Profile = -> Sketch015
  Suppress = false
  TreeRank = 249
  Type = 0
  _ProfileBasedVersion = 1
  _Version = 1
FEATURE [Sketcher::SketchObject] Sketch016
  FullyConstrained = true
  MapMode = 5
  Support = -> [Pocket007]
  TreeRank = 250
  sketch-geometry (1):
    g0: Circle CenterX=0 CenterY=0 CenterZ=0 NormalX=0 NormalY=0 NormalZ=1 AngleXU=0 Radius=3.5
  constraints (2):
    c: Coincident(g0,g-1)
    c: Diameter(g0) = 7
FEATURE [PartDesign::Pocket] Pocket008
  AddSubType = 1
  BaseFeature = -> Pocket007
  CheckUpToFaceLimits = true
  ClaimChildren = false
  Fit = 0
  FitJoin = 0
  InnerFit = 0
  InnerFitJoin = 0
  InnerTaperAngle = 0
  InnerTaperAngleRev = 0
  Length = 5
  Length2 = 100
  Linearize = true
  NewSolid = false
  Profile = -> Sketch016
  Suppress = false
  TreeRank = 251
  Type = 0
  _ProfileBasedVersion = 1
  _Version = 1
FEATURE [Sketcher::SketchObject] Sketch017
  FullyConstrained = true
  MapMode = 5
  Support = -> [Pocket008]
  TreeRank = 252
  sketch-geometry (9):
    g0: LineSegment [constr] StartX=-15.5 StartY=-15.5 StartZ=0 EndX=-15.5 EndY=15.5 EndZ=0
    g1: LineSegment [constr] StartX=-15.5 StartY=15.5 StartZ=0 EndX=15.5 EndY=15.5 EndZ=0
    g2: LineSegment [constr] StartX=15.5 StartY=15.5 StartZ=0 EndX=15.5 EndY=-15.5 EndZ=0
    g3: LineSegment [constr] StartX=15.5 StartY=-15.5 StartZ=0 EndX=-15.5 EndY=-15.5 EndZ=0
    g4: GeomPoint [constr] X=2e-16 Y=3e-16 Z=0
    g5: Circle CenterX=-15.5 CenterY=15.5 CenterZ=0 NormalX=0 NormalY=0 NormalZ=1 AngleXU=0 Radius=2.5
    g6: Circle CenterX=15.5 CenterY=15.5 CenterZ=0 NormalX=0 NormalY=0 NormalZ=1 AngleXU=0 Radius=2.5
    g7: Circle CenterX=15.5 CenterY=-15.5 CenterZ=0 NormalX=0 NormalY=0 NormalZ=1 AngleXU=0 Radius=2.5
    g8: Circle CenterX=-15.5 CenterY=-15.5 CenterZ=0 NormalX=0 NormalY=0 NormalZ=1 AngleXU=0 Radius=2.5
  constraints (20):
    c: Coincident(g0,g1)
    c: Coincident(g1,g2)
    c: Coincident(g2,g3)
    c: Coincident(g3,g0)
    c: Horizontal(g1)
    c: Horizontal(g3)
    c: Vertical(g0)
    c: Vertical(g2)
    c: Symmetric(g1,g0,g4)
    c: Coincident(g4,g-1)
    c: Equal(g1,g2)
    c: Distance(g1) = 31
    c: Coincident(g5,g0)
    c: Coincident(g6,g1)
    c: Coincident(g7,g2)
    c: Coincident(g8,g0)
    c: Equal(g8,g7)
    c: Equal(g7,g6)
    c: Equal(g6,g5)
    c: Diameter(g6) = 5
FEATURE [PartDesign::Hole] Hole
  AddSubType = 1
  BaseFeature = -> Pocket008
  ClaimChildren = false
  CustomThreadClearance = 0
  Depth = 25
  DepthType = 0
  Diameter = 3.4
  DrillForDepth = false
  DrillPoint = 1
  DrillPointAngle = 118
  Fit = 0
  FitJoin = 0
  HoleCutCountersinkAngle = 90
  HoleCutCustomValues = false
  HoleCutDepth = 0.4
  HoleCutDiameter = 6.9
  HoleCutType = 2
  InnerFit = 0
  InnerFitJoin = 0
  Linearize = true
  ModelThread = false
  NewSolid = false
  Profile = -> Sketch017
  Suppress = false
  Tapered = false
  TaperedAngle = 90
  ThreadClass = 0
  ThreadDepth = 25
  ThreadDepthType = 0
  ThreadDirection = 0
  ThreadFit = 0
  ThreadSize = 9
  ThreadType = 1
  Threaded = false
  TreeRank = 253
  UseCustomThreadClearance = false
  _ProfileBasedVersion = 1
FEATURE [PartDesign::Hole] Hole002
  AddSubType = 1
  BaseFeature = -> Hole
  ClaimChildren = false
  CustomThreadClearance = 0
  Depth = 10
  DepthType = 0
  Diameter = 3.4
  DrillForDepth = false
  DrillPoint = 1
  DrillPointAngle = 118
  Fit = 0
  FitJoin = 0
  HoleCutCountersinkAngle = 90
  HoleCutCustomValues = false
  HoleCutDepth = 0.4
  HoleCutDiameter = 6.9
  HoleCutType = 2
  InnerFit = 0
  InnerFitJoin = 0
  Linearize = true
  ModelThread = false
  NewSolid = false
  Profile = -> Binder
  Reversed = true
  Suppress = false
  Tapered = false
  TaperedAngle = 90
  ThreadClass = 0
  ThreadDepth = 10
  ThreadDepthType = 0
  ThreadDirection = 0
  ThreadFit = 0
  ThreadSize = 9
  ThreadType = 1
  Threaded = false
  TreeRank = 257
  UseCustomThreadClearance = false
  _ProfileBasedVersion = 1
FEATURE [PartDesign::Chamfer] Chamfer002
  AddSubType = 0
  Angle = 45
  Base = -> Hole002 [Edge3]
  BaseFeature = -> Hole002
  ChamferType = 0
  FlipDirection = false
  NewSolid = false
  Size = 2
  Size2 = 1
  SupportTransform = false
  Suppress = false
  TreeRank = 264
FEATURE [PartDesign::Body] Body007  label="Bottom-cap"
  AutoGroupSolids = false
  ClaimAllChildren = false
  ExportMode = 0
  Group = -> [ShapeBinder001,Pad015,Sketch015,Pocket007,Sketch016,Pocket008,Sketch017,Hole,Binder,Hole002,Chamfer002]
  Origin = -> Origin007
  Placement = pos=(0,0,-15) rot=(0,0,1;0rad)
  Tip = -> Chamfer002
  TreeRank = 243
  _ExportChildren = -> [Pad015,Pocket007,Pocket008,Hole,Hole002,Chamfer002]
  _GroupVersion = 1
COMPONENT P6 — recipe-attached ("Planet - Link 1", modeled in this document).
Construction recipe (the document's own serialized feature program — sketch geometry with constraints, then the solid features built on it; lengths are millimeters unless a unit is written):

FEATURE [Part::Part2DObjectPython] InvoluteGear005  label="s1-planet-gear"  # Draft 2D object (typed FeaturePython)
  ExternalGear = true
  HighPrecision = false
  Modules = 1.1
  NumberOfTeeth = 15
  PressureAngle = 20
  TreeRank = 160
  expr: Modules = <<sp>>.s1_module
  expr: NumberOfTeeth = <<sp>>.s1planet_teeth
FEATURE [Part::Part2DObjectPython] InvoluteGear004  label="s2-planet-gear"  # Draft 2D object (typed FeaturePython)
  ExternalGear = true
  HighPrecision = false
  Modules = 1
  NumberOfTeeth = 15
  Placement = pos=(0,0,10) rot=(0,0,1;0.174533rad)
  PressureAngle = 20
  TreeRank = 208
  expr: Modules = <<sp>>.s2_module
  expr: NumberOfTeeth = <<sp>>.s2planet_teeth
FEATURE [PartDesign::AdditiveHelix] Helix001
  AddSubType = 0
  Angle = 0
  Axis = (-3e-16,3e-16,1)
  Base = (0,0,0)
  ClaimChildren = false
  Fit = 0
  FitJoin = 0
  Growth = 0
  HasBeenEdited = true
  Height = 10
  InnerFit = 0
  InnerFitJoin = 0
  LeftHanded = true
  Linearize = true
  Mode = 0
  NewSolid = false
  Outside = false
  Pitch = 250
  Profile = -> InvoluteGear005
  ReferenceAxis = -> Z_Axis005
  Suppress = false
  TreeRank = 281
  Turns = 0.04
  _ProfileBasedVersion = 1
FEATURE [PartDesign::AdditiveHelix] Helix002
  AddSubType = 0
  Angle = 0
  Axis = (-3e-16,3e-16,1)
  Base = (0,0,0)
  BaseFeature = -> Helix001
  ClaimChildren = false
  Fit = 0
  FitJoin = 0
  Growth = 0
  HasBeenEdited = true
  Height = 11
  InnerFit = 0
  InnerFitJoin = 0
  LeftHanded = false
  Linearize = true
  Mode = 0
  NewSolid = false
  Outside = false
  Pitch = 250
  Profile = -> InvoluteGear004
  ReferenceAxis = -> Z_Axis005
  Suppress = false
  TreeRank = 282
  Turns = 0.044
  _ProfileBasedVersion = 1
FEATURE [Sketcher::SketchObject] Sketch023
  FullyConstrained = true
  MapMode = 5
  Placement = pos=(0,0,0) rot=(1,0,0;1.5708rad)
  Support = -> [XZ_Plane005]
  TreeRank = 289
  sketch-geometry (4):
    g0: LineSegment StartX=9.36 StartY=0 StartZ=0 EndX=9.36 EndY=1.4376 EndZ=0
    g1: LineSegment StartX=9.36 StartY=1.4376 StartZ=0 EndX=6.87 EndY=0 EndZ=0
    g2: LineSegment StartX=6.87 StartY=0 StartZ=0 EndX=8.25 EndY=0 EndZ=0
    g3: LineSegment StartX=8.25 StartY=0 StartZ=0 EndX=9.36 EndY=0 EndZ=0
  constraints (12):
    c: PointOnObject(g2,g-1)
    c: PointOnObject(g3,g-1)
    c: Coincident(g3,g0)
    c: Vertical(g0)
    c: Coincident(g0,g1)
    c: Coincident(g1,g2)
    c: Coincident(g2,g3)
    c: PointOnObject(g2,g-1)
    c: Distance(g2) = 1.38  'm*1.25'
    c: Distance(g3) = 1.11  'm'
    c: Angle(g2,g1) = 0.523599  'chamfer_angle'
    c: Distance(g-1,g2) = 8.25  'm*z'
FEATURE [PartDesign::Groove] Groove
  AddSubType = 1
  Angle = 360
  Axis = (0,-2e-16,1)
  Base = (0,0,0)
  BaseFeature = -> Helix002
  ClaimChildren = false
  Fit = 0
  FitJoin = 0
  InnerFit = 0
  InnerFitJoin = 0
  Linearize = true
  NewSolid = false
  Profile = -> Sketch023
  ReferenceAxis = -> Sketch023 [V_Axis]
  Suppress = false
  TreeRank = 290
  _ProfileBasedVersion = 1
FEATURE [PartDesign::Body] Body005  label="Planet"
  AutoGroupSolids = false
  ClaimAllChildren = false
  ExportMode = 0
  Group = -> [InvoluteGear005,InvoluteGear004,Helix001,Helix002,Sketch023,Groove]
  Origin = -> Origin005
  Placement = pos=(16.5,0,45) rot=(0,0,1;0rad)
  Tip = -> Groove
  TreeRank = 83
  _ExportChildren = -> [Helix001,Helix002,Groove]
  _GroupVersion = 1
  expr: Placement.Base.x = <<sp>>.E14
  expr: Placement.Base.y = <<sp>>.E15
COMPONENT P7 — same part as P6; its construction recipe is shown at P6.
PROVENANCE & LICENSES
A FreeCAD (.FCStd) document from a public repository crawl; recipes are the document's own serialized feature recipes (and, for linked parts, companion documents' recipes).
License: as declared in the source repository (recorded in the dataset sidecar).
